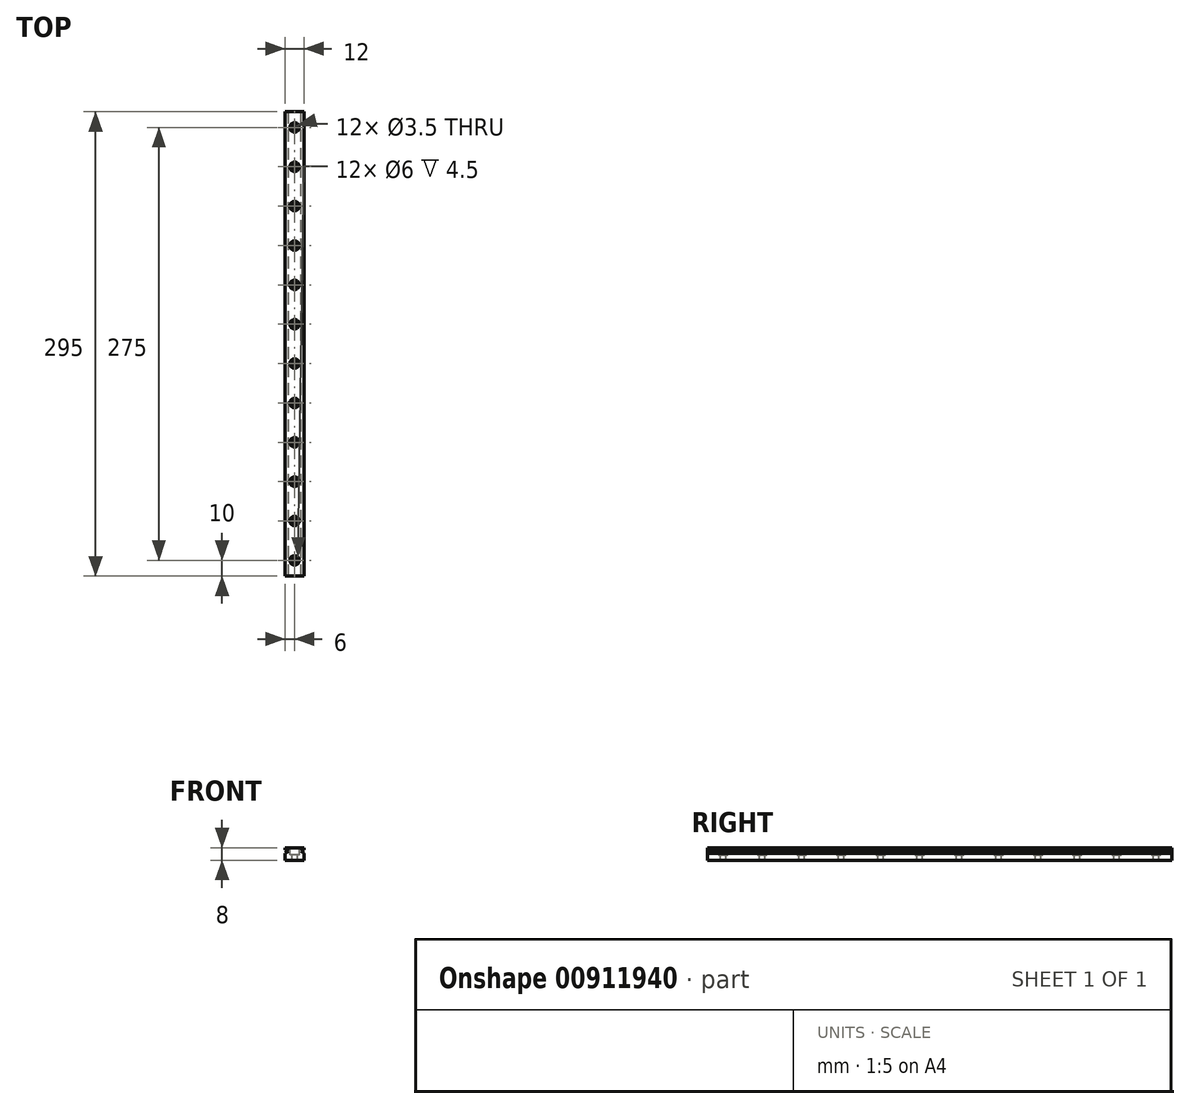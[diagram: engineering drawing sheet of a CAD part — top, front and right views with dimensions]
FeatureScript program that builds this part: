
annotation { "Feature Type Name" : "Feature", "Feature Type Description" : "" }
export const myFeature = defineFeature(function(context is Context, id is Id, definition is map)
    precondition{}
    {
        {
            var Q0;
            Q0=qCreatedBy(makeId("Front.planeOp"),FACE);
            var sketch = newSketch(context, id + "F0", { "sketchPlane" : qUnion([Q0])});
            skLineSegment(sketch, "E0", {"start": v(-6, 0) * mm, "end": v(6, 0) * mm});
            skLineSegment(sketch, "E1", {"start": v(6, 0) * mm, "end": v(6, 4.5) * mm});
            skLineSegment(sketch, "E2", {"start": v(6, 4.5) * mm, "end": v(4, 5.5) * mm});
            skLineSegment(sketch, "E3", {"start": v(4, 5.5) * mm, "end": v(6, 6.5) * mm});
            skLineSegment(sketch, "E4", {"start": v(6, 6.5) * mm, "end": v(6, 8) * mm});
            skLineSegment(sketch, "E5", {"start": v(6, 8) * mm, "end": v(-6, 8) * mm});
            skLineSegment(sketch, "E6", {"start": v(0, 8) * mm, "end": v(0, 0) * mm, "construction": true});
            skLineSegment(sketch, "E7.MirrorCS", {"start": v(-6, 6.5) * mm, "end": v(-6, 8) * mm});
            skLineSegment(sketch, "E8.MirrorCS", {"start": v(-4, 5.5) * mm, "end": v(-6, 6.5) * mm});
            skLineSegment(sketch, "E9.MirrorCS", {"start": v(-6, 4.5) * mm, "end": v(-4, 5.5) * mm});
            skLineSegment(sketch, "E10.MirrorCS", {"start": v(-6, 0) * mm, "end": v(-6, 4.5) * mm});
            skSolve(sketch);
        }
        {
            var Q0;
            Q0 = qSketchRegion(id + "F0", true);
            extrude(context, id + "F1", {"entities" : qUnion([Q0]), "depth" : 295 * mm, "offsetDistance" : 25 * mm});
        }
        {
            var Q0;
            Q0=makeQuery(id+"F1.opExtrude","SWEPT_FACE",FACE,{"disambiguationData":[OSD([sQuery(id+"F0.wireOp",EDGE,"E5")])]});
            var sketch = newSketch(context, id + "F2", { "sketchPlane" : qUnion([Q0])});
            skPoint(sketch, "E11", {"position": v(0, -285) * mm});
            skLineSegment(sketch, "E12", {"start": v(0, -295) * mm, "end": v(0, -285) * mm, "construction": true});
            skPoint(sketch, "E13.0.1.0", {"position": v(0, -260) * mm});
            skPoint(sketch, "E13.0.2.0", {"position": v(0, -235) * mm});
            skPoint(sketch, "E13.0.3.0", {"position": v(0, -210) * mm});
            skPoint(sketch, "E13.0.4.0", {"position": v(0, -185) * mm});
            skPoint(sketch, "E13.0.5.0", {"position": v(0, -160) * mm});
            skPoint(sketch, "E13.0.6.0", {"position": v(0, -135) * mm});
            skPoint(sketch, "E13.0.7.0", {"position": v(0, -110) * mm});
            skPoint(sketch, "E13.0.8.0", {"position": v(0, -85) * mm});
            skPoint(sketch, "E13.0.9.0", {"position": v(0, -60) * mm});
            skPoint(sketch, "E13.0.10.0", {"position": v(0, -35) * mm});
            skPoint(sketch, "E13.0.11.0", {"position": v(0, -10) * mm});
            skLineSegment(sketch, "E13.direction1", {"start": v(0, -285) * mm, "end": v(25, -285) * mm, "construction": true});
            skLineSegment(sketch, "E13.direction2", {"start": v(0, -285) * mm, "end": v(0, -260) * mm, "construction": true});
            skSolve(sketch);
        }
        {
            var Q0;
            Q0=sQuery(id+"F2.wireOp",VERTEX,"E11");
            var Q1;
            Q1=sQuery(id+"F2.wireOp",VERTEX,"E13.0.1.0");
            var Q2;
            Q2=sQuery(id+"F2.wireOp",VERTEX,"E13.0.2.0");
            var Q3;
            Q3=sQuery(id+"F2.wireOp",VERTEX,"E13.0.3.0");
            var Q4;
            Q4=sQuery(id+"F2.wireOp",VERTEX,"E13.0.4.0");
            var Q5;
            Q5=sQuery(id+"F2.wireOp",VERTEX,"E13.0.5.0");
            var Q6;
            Q6=sQuery(id+"F2.wireOp",VERTEX,"E13.0.6.0");
            var Q7;
            Q7=sQuery(id+"F2.wireOp",VERTEX,"E13.0.7.0");
            var Q8;
            Q8=sQuery(id+"F2.wireOp",VERTEX,"E13.0.8.0");
            var Q9;
            Q9=sQuery(id+"F2.wireOp",VERTEX,"E13.0.11.0");
            var Q10;
            Q10=sQuery(id+"F2.wireOp",VERTEX,"E13.0.10.0");
            var Q11;
            Q11=sQuery(id+"F2.wireOp",VERTEX,"E13.0.9.0");
            var Q12;
            Q12=makeQuery(id+"F1.opExtrude","SWEPT_BODY",BODY,{"disambiguationData":[OSD([sQuery(id+"F0.wireOp",EDGE,"E0"),sQuery(id+"F0.wireOp",EDGE,"E1"),sQuery(id+"F0.wireOp",EDGE,"E2"),sQuery(id+"F0.wireOp",EDGE,"E3"),sQuery(id+"F0.wireOp",EDGE,"E4"),sQuery(id+"F0.wireOp",EDGE,"E5"),sQuery(id+"F0.wireOp",EDGE,"E7.MirrorCS"),sQuery(id+"F0.wireOp",EDGE,"E8.MirrorCS"),sQuery(id+"F0.wireOp",EDGE,"E9.MirrorCS"),sQuery(id+"F0.wireOp",EDGE,"E10.MirrorCS")])]});
            hole(context, id + "F3", {"style" : HoleStyle.C_BORE, "endStyle" : HoleEndStyle.BLIND, "holeDiameter" : 3.5 * mm, "cBoreDiameter" : 6 * mm, "cBoreDepth" : 4.5 * mm, "majorDiameter" : 4 * mm, "holeDepth" : 20 * mm, "isTappedThrough" : true, "tappedDepth" : 12 * mm, "tapClearance" : 3, "locations" : qUnion([Q0, Q1, Q2, Q3, Q4, Q5, Q6, Q7, Q8, Q9, Q10, Q11]), "scope" : qUnion([Q12])});
        }
    });
